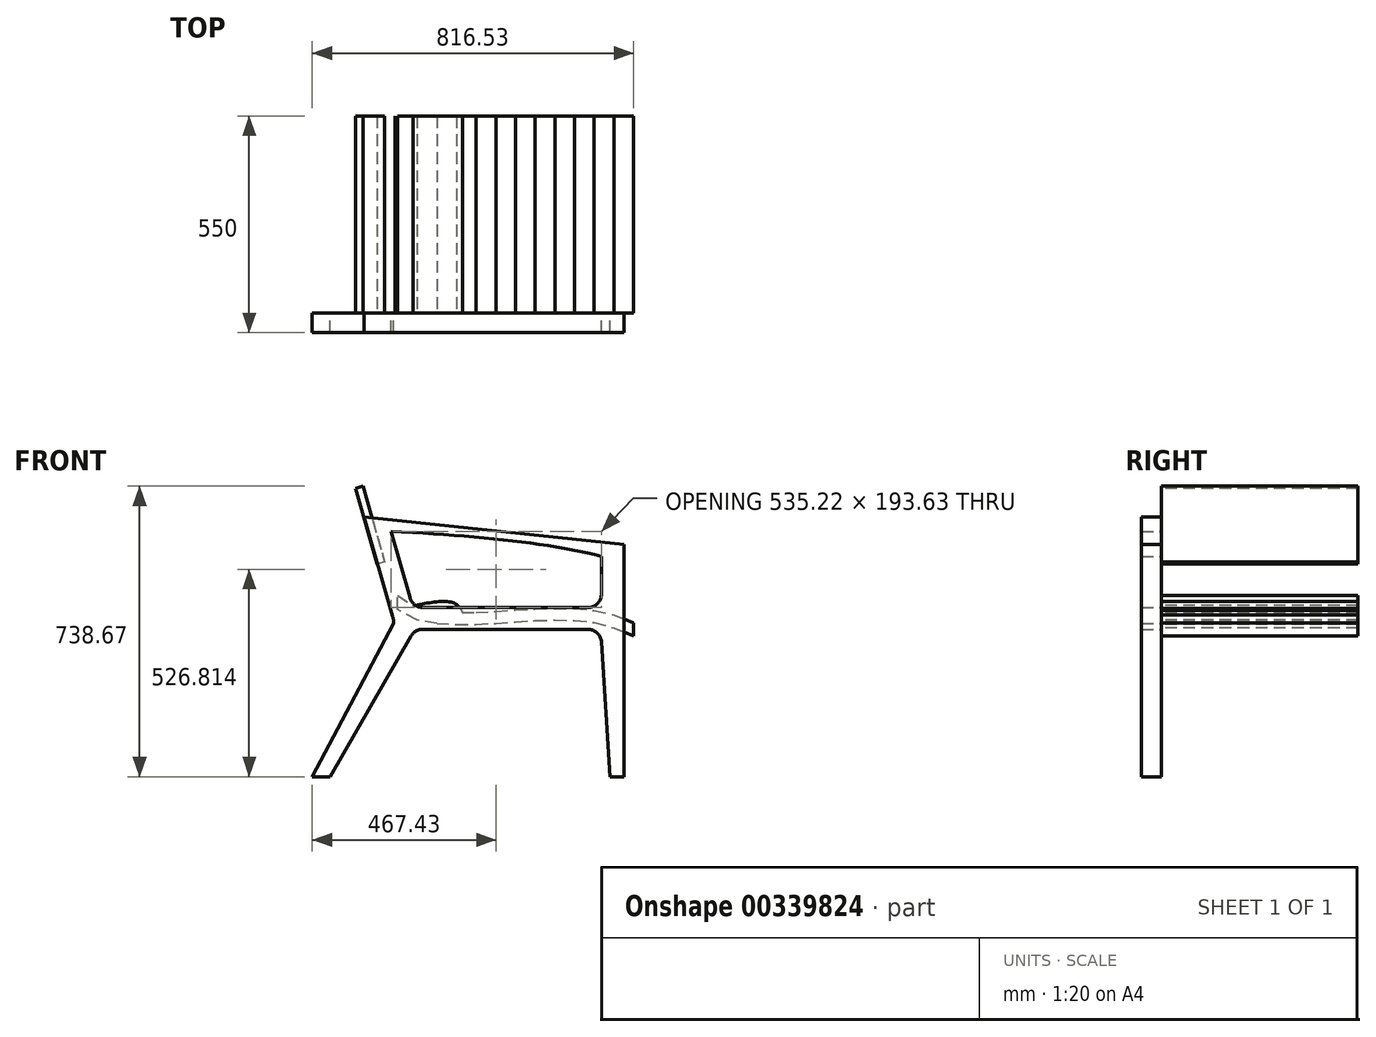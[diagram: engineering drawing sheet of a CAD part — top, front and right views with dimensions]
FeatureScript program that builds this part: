
annotation { "Feature Type Name" : "Feature", "Feature Type Description" : "" }
export const myFeature = defineFeature(function(context is Context, id is Id, definition is map)
    precondition{}
    {
        {
            var Q0;
            Q0=qCreatedBy(makeId("Front.planeOp"),FACE);
            var sketch = newSketch(context, id + "F0", { "sketchPlane" : qUnion([Q0])});
            skLineSegment(sketch, "E0", {"start": v(-160.06, 0) * mm, "end": v(258.26, 0) * mm});
            skLineSegment(sketch, "E1.0", {"start": v(-160.06, -55) * mm, "end": v(258.26, -55) * mm});
            skLineSegment(sketch, "E2.0", {"start": v(349.94, 160) * mm, "end": v(349.94, -430) * mm});
            skLineSegment(sketch, "E3", {"start": v(-193.7, 25.35) * mm, "end": v(-241.96, 193.63) * mm});
            skLineSegment(sketch, "E4", {"start": v(-190.37, -72.5) * mm, "end": v(-396.78, -430) * mm});
            skLineSegment(sketch, "E5.0", {"start": v(349.73, -430) * mm, "end": v(348.96, -430) * mm});
            skLineSegment(sketch, "E6", {"start": v(349.73, -430) * mm, "end": v(349.94, -430) * mm});
            skLineSegment(sketch, "E7", {"start": v(-396.78, -430) * mm, "end": v(-441.78, -430) * mm});
            skLineSegment(sketch, "E8.0", {"start": v(-237.12, -22.78) * mm, "end": v(-309.6, 230) * mm});
            skArc(sketch, "E9.filletArc", {"start": v(-160.06, -55) * mm, "mid": v(-177.56, -59.69) * mm, "end": v(-190.37, -72.5) * mm});
            skArc(sketch, "E10.filletArc", {"start": v(-235.33, -40.37) * mm, "mid": v(-235.44, -31.5) * mm, "end": v(-237.12, -22.78) * mm});
            skArc(sketch, "E11.filletArc", {"start": v(-193.7, 25.35) * mm, "mid": v(-181.13, 7.05) * mm, "end": v(-160.06, 0) * mm});
            skLineSegment(sketch, "E12", {"start": v(-235.33, -40.37) * mm, "end": v(-441.78, -430) * mm});
            skLineSegment(sketch, "E13", {"start": v(293.26, 35) * mm, "end": v(293.26, 130) * mm});
            skFitSpline(sketch, "E14", {"points": [v(-241.96, 193.63) * mm, v(293.26, 130) * mm, v(482.35, 46.07) * mm], "startDerivative": vector(1025.62, -54.46) * mm, "endDerivative": vector(365.11, -259.67) * mm});
            skLineSegment(sketch, "E15", {"start": v(349.94, 160) * mm, "end": v(293.26, 130) * mm});
            skLineSegment(sketch, "E16", {"start": v(-309.6, 230) * mm, "end": v(349.94, 160) * mm});
            skLineSegment(sketch, "E17", {"start": v(-241.96, 193.63) * mm, "end": v(-309.6, 230) * mm});
            skLineSegment(sketch, "E18", {"start": v(349.94, -430) * mm, "end": v(314.94, -430) * mm});
            skLineSegment(sketch, "E19", {"start": v(293.2, -87.78) * mm, "end": v(314.94, -430) * mm});
            skArc(sketch, "E20", {"start": v(-160.06, 0) * mm, "mid": v(-166.74, -27.5) * mm, "end": v(-160.06, -55) * mm});
            skArc(sketch, "E21.filletArc", {"start": v(258.26, 0) * mm, "mid": v(283, 10.25) * mm, "end": v(293.26, 35) * mm});
            skArc(sketch, "E22.filletArc", {"start": v(293.2, -87.78) * mm, "mid": v(282.21, -64.48) * mm, "end": v(258.26, -55) * mm});
            skArc(sketch, "E23", {"start": v(258.26, -55) * mm, "mid": v(264.93, -27.5) * mm, "end": v(258.26, 0) * mm});
            skLineSegment(sketch, "E24", {"start": v(-396.78, -430) * mm, "end": v(314.94, -430) * mm, "construction": true});
            skLineSegment(sketch, "E25", {"start": v(-235.33, -31.5) * mm, "end": v(-358.73, -31.5) * mm});
            skPoint(sketch, "E25.startSnap0", {"position": v(-235.44, -31.5) * mm});
            skSolve(sketch);
        }
        {
            var Q0;
            Q0=qCreatedBy(makeId("Front.planeOp"),FACE);
            var sketch = newSketch(context, id + "F1", { "sketchPlane" : qUnion([Q0])});
            skLineSegment(sketch, "E26", {"start": v(-332.25, 303.17) * mm, "end": v(-277.26, 110.88) * mm});
            skLineSegment(sketch, "E27", {"start": v(-313.02, 308.67) * mm, "end": v(-258.03, 116.38) * mm});
            skPoint(sketch, "E28.startDerivative.orphan", {"position": v(70.06, -25.15) * mm});
            skLineSegment(sketch, "E29.0", {"start": v(324.75, -19.2) * mm, "end": v(324.75, -51.55) * mm});
            skLineSegment(sketch, "E30.0", {"start": v(274.75, -7.22) * mm, "end": v(274.75, -38.07) * mm});
            skLineSegment(sketch, "E31.0", {"start": v(224.75, -2.52) * mm, "end": v(224.75, -32.65) * mm});
            skLineSegment(sketch, "E32.0", {"start": v(174.75, -1.66) * mm, "end": v(174.75, -31.67) * mm});
            skLineSegment(sketch, "E33.0", {"start": v(124.75, -3.2) * mm, "end": v(124.75, -33.25) * mm});
            skLineSegment(sketch, "E34.0", {"start": v(24.75, -10.03) * mm, "end": v(24.75, -40.06) * mm});
            skLineSegment(sketch, "E35.0", {"start": v(-25.25, -12.37) * mm, "end": v(-25.25, -42.37) * mm});
            skLineSegment(sketch, "E36.0", {"start": v(-75.25, -12.7) * mm, "end": v(-75.25, -42.7) * mm});
            skLineSegment(sketch, "E37.0", {"start": v(-175.25, -1.37) * mm, "end": v(-175.25, -31.8) * mm});
            skFitSpline(sketch, "E38", {"points": [v(-226.6, 30.57) * mm, v(-225.69, 3.87) * mm, v(-86.7, 13.22) * mm, v(-52.2, -57) * mm], "startDerivative": vector(-26.4, -144.35) * mm, "endDerivative": vector(27.59, -264.6) * mm});
            skLineSegment(sketch, "E39.0", {"start": v(-231.59, -1.43) * mm, "end": v(-231.59, -1.44) * mm});
            skLineSegment(sketch, "E40", {"start": v(-175.25, -1.37) * mm, "end": v(-125.25, -9.86) * mm});
            skLineSegment(sketch, "E41", {"start": v(-125.25, -9.86) * mm, "end": v(-75.25, -12.7) * mm});
            skLineSegment(sketch, "E42", {"start": v(-75.25, -12.7) * mm, "end": v(-25.25, -12.37) * mm});
            skLineSegment(sketch, "E43", {"start": v(-25.25, -12.37) * mm, "end": v(24.75, -10.03) * mm});
            skLineSegment(sketch, "E44", {"start": v(24.75, -10.03) * mm, "end": v(74.75, -6.35) * mm});
            skLineSegment(sketch, "E45", {"start": v(74.75, -6.35) * mm, "end": v(124.75, -3.2) * mm});
            skLineSegment(sketch, "E46", {"start": v(124.75, -3.2) * mm, "end": v(174.75, -1.66) * mm});
            skLineSegment(sketch, "E47", {"start": v(174.75, -1.66) * mm, "end": v(224.75, -2.52) * mm});
            skLineSegment(sketch, "E48", {"start": v(224.75, -2.52) * mm, "end": v(274.75, -7.22) * mm});
            skLineSegment(sketch, "E49", {"start": v(274.75, -7.22) * mm, "end": v(324.75, -19.2) * mm});
            skLineSegment(sketch, "E50", {"start": v(324.75, -19.2) * mm, "end": v(374.75, -39.4) * mm});
            skLineSegment(sketch, "E51.0", {"start": v(324.75, -51.55) * mm, "end": v(374.75, -71.76) * mm});
            skLineSegment(sketch, "E51.6", {"start": v(-231.6, -1.43) * mm, "end": v(-231.59, -1.43) * mm});
            skLineSegment(sketch, "E51.7", {"start": v(-75.25, -42.7) * mm, "end": v(-25.25, -42.37) * mm});
            skLineSegment(sketch, "E52", {"start": v(-231.6, -1.43) * mm, "end": v(-231.59, -1.44) * mm});
            skLineSegment(sketch, "E53.trimOffspring", {"start": v(-175.25, -52.88) * mm, "end": v(-175.25, -54.07) * mm});
            skLineSegment(sketch, "E54.trimOffspring", {"start": v(174.75, -52.88) * mm, "end": v(174.75, -54.07) * mm});
            skLineSegment(sketch, "E55.trimOffspring", {"start": v(124.75, -52.88) * mm, "end": v(124.75, -54.07) * mm});
            skLineSegment(sketch, "E56.trimOffspring", {"start": v(74.75, -52.88) * mm, "end": v(74.75, -54.07) * mm});
            skLineSegment(sketch, "E57", {"start": v(-125.25, -9.86) * mm, "end": v(-125.25, -39.9) * mm});
            skLineSegment(sketch, "E58", {"start": v(74.75, -6.35) * mm, "end": v(74.75, -36.28) * mm});
            skLineSegment(sketch, "E59", {"start": v(-125.25, -39.9) * mm, "end": v(-175.25, -31.8) * mm});
            skLineSegment(sketch, "E60", {"start": v(-125.25, -39.9) * mm, "end": v(-75.25, -42.7) * mm});
            skPoint(sketch, "E61.orphan", {"position": v(76.8, -36.28) * mm});
            skLineSegment(sketch, "E62", {"start": v(-25.25, -42.37) * mm, "end": v(24.75, -40.06) * mm});
            skLineSegment(sketch, "E63", {"start": v(24.75, -40.06) * mm, "end": v(74.75, -36.28) * mm});
            skLineSegment(sketch, "E64", {"start": v(74.75, -36.28) * mm, "end": v(124.75, -33.25) * mm});
            skLineSegment(sketch, "E65", {"start": v(124.75, -33.25) * mm, "end": v(174.75, -31.67) * mm});
            skLineSegment(sketch, "E66", {"start": v(174.75, -31.67) * mm, "end": v(224.75, -32.65) * mm});
            skLineSegment(sketch, "E67", {"start": v(224.75, -32.65) * mm, "end": v(274.75, -38.07) * mm});
            skLineSegment(sketch, "E68", {"start": v(274.75, -38.07) * mm, "end": v(324.75, -51.55) * mm});
            skLineSegment(sketch, "E69", {"start": v(-225.25, 30.57) * mm, "end": v(-175.25, -1.37) * mm});
            skLineSegment(sketch, "E70", {"start": v(-175.25, -31.8) * mm, "end": v(-225.25, -4.67) * mm});
            skLineSegment(sketch, "E71", {"start": v(-225.25, -4.67) * mm, "end": v(-225.25, 30.57) * mm});
            skLineSegment(sketch, "E72", {"start": v(374.75, -39.4) * mm, "end": v(374.75, -71.76) * mm});
            skLineSegment(sketch, "E73", {"start": v(-258.03, 116.38) * mm, "end": v(-277.26, 110.88) * mm});
            skLineSegment(sketch, "E74.0", {"start": v(-271.78, 164.45) * mm, "end": v(-291, 158.96) * mm});
            skLineSegment(sketch, "E75.0", {"start": v(-285.53, 212.53) * mm, "end": v(-304.76, 207.03) * mm});
            skLineSegment(sketch, "E76.0", {"start": v(-299.28, 260.6) * mm, "end": v(-318.5, 255.1) * mm});
            skLineSegment(sketch, "E77.0", {"start": v(-313.02, 308.67) * mm, "end": v(-332.25, 303.17) * mm});
            skSolve(sketch);
        }
        {
            var Q0;
            Q0=qSketchRegion(id+"F1",true);
            extrude(context, id + "F2", {"entities" : qUnion([Q0]), "oppositeDirection" : true, "offsetDistance" : 25 * mm, "depth" : 500 * mm});
        }
        {
            var Q0;
            Q0=qSketchRegion(id+"F0",true);
            extrude(context, id + "F3", {"entities" : qUnion([Q0]), "offsetDistance" : 25 * mm, "depth" : 50 * mm});
        }
    });
